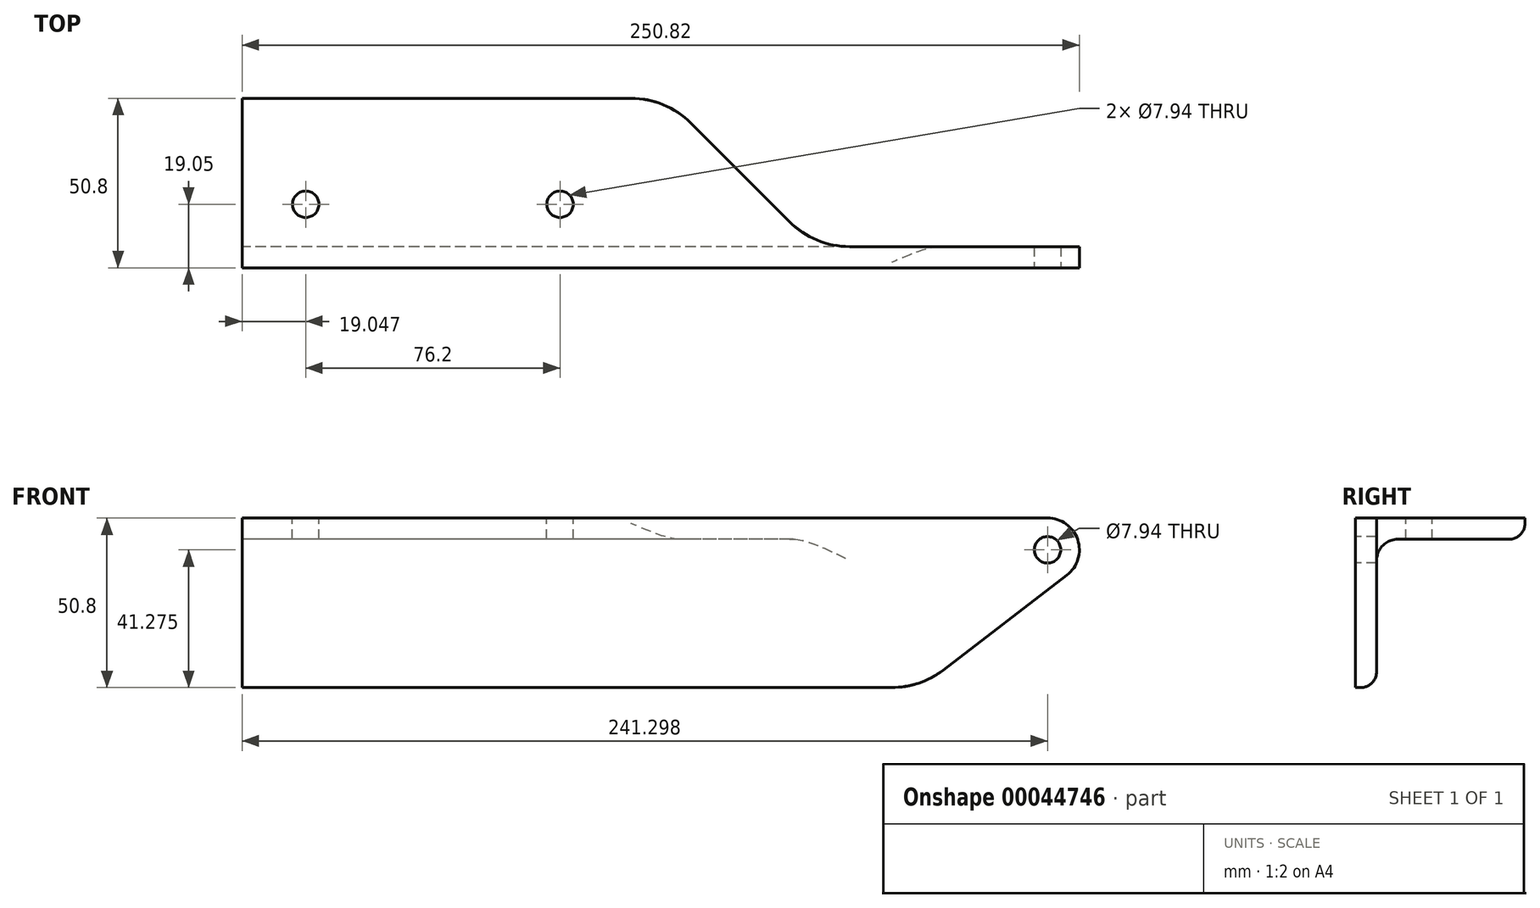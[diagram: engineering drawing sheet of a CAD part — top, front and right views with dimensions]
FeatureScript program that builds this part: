
annotation { "Feature Type Name" : "Feature", "Feature Type Description" : "" }
export const myFeature = defineFeature(function(context is Context, id is Id, definition is map)
    precondition{}
    {
        {
            var Q0;
            Q0=qCreatedBy(makeId("Right.planeOp"),FACE);
            var sketch = newSketch(context, id + "F0", { "sketchPlane" : qUnion([Q0])});
            skLineSegment(sketch, "E0", {"start": v(0, 0) * mm, "end": v(50.8, 0) * mm});
            skLineSegment(sketch, "E1", {"start": v(0, 0) * mm, "end": v(0, -50.8) * mm});
            skLineSegment(sketch, "E2.0", {"start": v(12.7, -6.35) * mm, "end": v(46.04, -6.35) * mm});
            skLineSegment(sketch, "E2.1", {"start": v(6.35, -12.7) * mm, "end": v(6.35, -46.04) * mm});
            skPoint(sketch, "E3.visualSharp", {"position": v(6.35, -6.35) * mm});
            skArc(sketch, "E3.filletArc", {"start": v(12.7, -6.35) * mm, "mid": v(8.2, -8.2) * mm, "end": v(6.35, -12.7) * mm});
            skLineSegment(sketch, "E4", {"start": v(1.59, -50.8) * mm, "end": v(0, -50.8) * mm});
            skLineSegment(sketch, "E5", {"start": v(50.8, -1.59) * mm, "end": v(50.8, 0) * mm});
            skPoint(sketch, "E6.visualSharp", {"position": v(50.8, -6.35) * mm});
            skArc(sketch, "E6.filletArc", {"start": v(46.04, -6.35) * mm, "mid": v(49.4, -4.96) * mm, "end": v(50.8, -1.59) * mm});
            skPoint(sketch, "E7.visualSharp", {"position": v(6.35, -50.8) * mm});
            skArc(sketch, "E7.filletArc", {"start": v(1.59, -50.8) * mm, "mid": v(4.96, -49.4) * mm, "end": v(6.35, -46.04) * mm});
            skSolve(sketch);
        }
        {
            var Q0;
            Q0 = qSketchRegion(id + "F0", true);
            extrude(context, id + "F1", {"entities" : qUnion([Q0]), "endBound" : BoundingType.SYMMETRIC, "depth" : 250.82 * mm});
        }
        {
            var Q0;
            Q0=makeQuery(id+"F1.opExtrude","SWEPT_FACE",FACE,{"disambiguationData":[OSD([sQuery(id+"F0.wireOp",EDGE,"E0")])]});
            var sketch = newSketch(context, id + "F2", { "sketchPlane" : qUnion([Q0])});
            skLineSegment(sketch, "E8.0", {"start": v(125.41, 0) * mm, "end": v(-125.41, 0) * mm, "construction": true});
            skLineSegment(sketch, "E9.0", {"start": v(125.41, 19.05) * mm, "end": v(-125.41, 19.05) * mm, "construction": true});
            skLineSegment(sketch, "E10.0", {"start": v(-125.41, 0) * mm, "end": v(-125.41, 50.8) * mm, "construction": true});
            skLineSegment(sketch, "E11.0", {"start": v(-106.36, 0) * mm, "end": v(-106.36, 50.8) * mm, "construction": true});
            skLineSegment(sketch, "E12.0", {"start": v(-30.16, 0) * mm, "end": v(-30.16, 50.8) * mm, "construction": true});
            skPoint(sketch, "E13", {"position": v(-106.36, 19.05) * mm});
            skPoint(sketch, "E14", {"position": v(-30.16, 19.05) * mm});
            skSolve(sketch);
        }
        {
            var Q0;
            Q0=sQuery(id+"F2.wireOp",VERTEX,"E13");
            var Q1;
            Q1=sQuery(id+"F2.wireOp",VERTEX,"E14");
            var Q2;
            Q2=makeQuery(id+"F1.opExtrude","SWEPT_BODY",BODY,{"disambiguationData":[OSD([sQuery(id+"F0.wireOp",EDGE,"E0"),sQuery(id+"F0.wireOp",EDGE,"E1"),sQuery(id+"F0.wireOp",EDGE,"E2.0"),sQuery(id+"F0.wireOp",EDGE,"E2.1"),sQuery(id+"F0.wireOp",EDGE,"E3.filletArc"),sQuery(id+"F0.wireOp",EDGE,"E4"),sQuery(id+"F0.wireOp",EDGE,"E5"),sQuery(id+"F0.wireOp",EDGE,"E6.filletArc"),sQuery(id+"F0.wireOp",EDGE,"E7.filletArc")])]});
            hole(context, id + "F3", {"style" : HoleStyle.SIMPLE, "holeDiameter" : 7.94 * mm, "endStyle" : HoleEndStyle.THROUGH, "locations" : qUnion([Q0, Q1]), "scope" : qUnion([Q2])});
        }
        {
            var Q0;
            Q0=makeQuery(id+"F1.opExtrude","SWEPT_FACE",FACE,{"disambiguationData":[OSD([sQuery(id+"F0.wireOp",EDGE,"E0")])]});
            var sketch = newSketch(context, id + "F4", { "sketchPlane" : qUnion([Q0])});
            skLineSegment(sketch, "E15.0", {"start": v(125.41, 6.35) * mm, "end": v(46.04, 6.35) * mm});
            skLineSegment(sketch, "E16.0", {"start": v(-125.41, 0) * mm, "end": v(-125.41, 50.8) * mm, "construction": true});
            skLineSegment(sketch, "E17.0", {"start": v(1.59, 0) * mm, "end": v(1.59, 50.8) * mm, "construction": true});
            skLineSegment(sketch, "E18.0", {"start": v(46.04, 0) * mm, "end": v(46.04, 50.8) * mm, "construction": true});
            skLineSegment(sketch, "E19", {"start": v(46.04, 6.35) * mm, "end": v(1.59, 50.8) * mm});
            skLineSegment(sketch, "E20", {"start": v(1.59, 50.8) * mm, "end": v(125.41, 50.8) * mm});
            skLineSegment(sketch, "E21", {"start": v(125.41, 50.8) * mm, "end": v(125.41, 6.35) * mm});
            skPoint(sketch, "E22.orphan", {"position": v(-125.41, 6.35) * mm});
            skSolve(sketch);
        }
        {
            var Q0;
            Q0 = qSketchRegion(id + "F4", true);
            extrude(context, id + "F5", {"entities" : qUnion([Q0]), "operationType" : NewBodyOperationType.REMOVE, "endBound" : BoundingType.THROUGH_ALL, "oppositeDirection" : true, "depth" : 25.4 * mm});
        }
        {
            var Q0;
            Q0=makeQuery(id+"F1.opExtrude","SWEPT_FACE",FACE,{"disambiguationData":[OSD([sQuery(id+"F0.wireOp",EDGE,"E0")])]});
            var sketch = newSketch(context, id + "F6", { "sketchPlane" : qUnion([Q0])});
            skLineSegment(sketch, "E23.0", {"start": v(-8.93, 50.8) * mm, "end": v(-125.41, 50.8) * mm});
            skLineSegment(sketch, "E24.0", {"start": v(46.04, 6.35) * mm, "end": v(9.03, 43.36) * mm});
            skLineSegment(sketch, "E25.rect.bottom", {"start": v(-21.33, 63.74) * mm, "end": v(24.5, 63.74) * mm});
            skLineSegment(sketch, "E25.rect.top", {"start": v(14.53, 37.86) * mm, "end": v(24.5, 37.86) * mm});
            skLineSegment(sketch, "E25.rect.left", {"start": v(-21.33, 63.74) * mm, "end": v(-21.33, 50.8) * mm});
            skLineSegment(sketch, "E25.rect.right", {"start": v(24.5, 63.74) * mm, "end": v(24.5, 37.86) * mm});
            skPoint(sketch, "E25.rect.middle", {"position": v(1.59, 50.8) * mm});
            skArc(sketch, "E26.filletArc", {"start": v(9.03, 43.36) * mm, "mid": v(0.79, 48.87) * mm, "end": v(-8.93, 50.8) * mm});
            skPoint(sketch, "E27.orphan", {"position": v(-21.33, 37.86) * mm});
            skSolve(sketch);
        }
        {
            var Q0;
            Q0 = qSketchRegion(id + "F6", true);
            extrude(context, id + "F7", {"entities" : qUnion([Q0]), "operationType" : NewBodyOperationType.REMOVE, "endBound" : BoundingType.THROUGH_ALL, "oppositeDirection" : true, "depth" : 25.4 * mm});
        }
        {
            var Q0;
            Q0=makeQuery(id+"F5.boolean.opBoolean","COPY",EDGE,{"derivedFrom":makeQuery(id+"F5.opExtrude","SWEPT_EDGE",EDGE,{"disambiguationData":[OSD([sQuery(id+"F4.wireOp",EDGE,"E15.0"),sQuery(id+"F4.wireOp",EDGE,"E19")])]})});
            fillet(context, id + "F8", {"entities" : qUnion([Q0]), "radius" : 25.4 * mm, "tangentPropagation" : true, "allowEdgeOverflow" : false});
        }
        {
            var Q0;
            Q0=makeQuery(id+"F1.opExtrude","SWEPT_FACE",FACE,{"disambiguationData":[OSD([sQuery(id+"F0.wireOp",EDGE,"E1")])]});
            var sketch = newSketch(context, id + "F9", { "sketchPlane" : qUnion([Q0])});
            skLineSegment(sketch, "E28.0", {"start": v(-125.41, 0) * mm, "end": v(-125.41, -50.8) * mm, "construction": true});
            skLineSegment(sketch, "E29.0", {"start": v(115.89, 0) * mm, "end": v(115.89, -50.8) * mm, "construction": true});
            skLineSegment(sketch, "E30.0", {"start": v(125.41, -9.53) * mm, "end": v(-125.41, -9.53) * mm, "construction": true});
            skArc(sketch, "E31", {"start": v(115.89, -19.05) * mm, "mid": v(125.41, -9.53) * mm, "end": v(115.89, 0) * mm});
            skLineSegment(sketch, "E32.0", {"start": v(77.79, 0) * mm, "end": v(77.79, -50.8) * mm});
            skLineSegment(sketch, "E33.0", {"start": v(125.41, -50.8) * mm, "end": v(-125.41, -50.8) * mm});
            skLineSegment(sketch, "E34", {"start": v(77.79, -50.8) * mm, "end": v(121.69, -17.08) * mm});
            skLineSegment(sketch, "E35", {"start": v(115.89, 0) * mm, "end": v(115.89, 14.21) * mm});
            skLineSegment(sketch, "E36", {"start": v(115.89, 14.21) * mm, "end": v(141.57, 14.21) * mm});
            skLineSegment(sketch, "E37", {"start": v(141.57, 14.21) * mm, "end": v(141.57, -61.2) * mm});
            skLineSegment(sketch, "E38", {"start": v(141.57, -61.2) * mm, "end": v(77.79, -61.2) * mm});
            skLineSegment(sketch, "E39", {"start": v(77.79, -61.2) * mm, "end": v(77.79, -50.8) * mm});
            skSolve(sketch);
        }
        {
            var Q0;
            Q0 = qSketchRegion(id + "F9", true);
            extrude(context, id + "F10", {"entities" : qUnion([Q0]), "operationType" : NewBodyOperationType.REMOVE, "endBound" : BoundingType.THROUGH_ALL, "oppositeDirection" : true, "depth" : 25.4 * mm});
        }
        {
            var Q0;
            {var subQ2=sQuery(id+"F9.wireOp",EDGE,"E32.0");Q0=makeQuery(id+"F9.imprint","IMPRINT",FACE,{"disambiguationData":[TD([[makeQuery(id+"F9.imprint","IMPRINT",EDGE,{"derivedFrom":subQ2}),1.0]])]});}
            var sketch = newSketch(context, id + "F11", { "sketchPlane" : qUnion([Q0])});
            skLineSegment(sketch, "E40.0", {"start": v(125.41, -9.53) * mm, "end": v(-125.41, -9.53) * mm, "construction": true});
            skLineSegment(sketch, "E41.0", {"start": v(115.89, 0) * mm, "end": v(115.89, -50.8) * mm, "construction": true});
            skPoint(sketch, "E42", {"position": v(115.89, -9.53) * mm});
            skSolve(sketch);
        }
        {
            var Q0;
            Q0=sQuery(id+"F11.wireOp",VERTEX,"E42");
            var Q1;
            Q1=makeQuery(id+"F1.opExtrude","SWEPT_BODY",BODY,{"disambiguationData":[OSD([sQuery(id+"F0.wireOp",EDGE,"E0"),sQuery(id+"F0.wireOp",EDGE,"E1"),sQuery(id+"F0.wireOp",EDGE,"E2.0"),sQuery(id+"F0.wireOp",EDGE,"E2.1"),sQuery(id+"F0.wireOp",EDGE,"E3.filletArc"),sQuery(id+"F0.wireOp",EDGE,"E4"),sQuery(id+"F0.wireOp",EDGE,"E5"),sQuery(id+"F0.wireOp",EDGE,"E6.filletArc"),sQuery(id+"F0.wireOp",EDGE,"E7.filletArc")])]});
            hole(context, id + "F12", {"style" : HoleStyle.SIMPLE, "holeDiameter" : 7.94 * mm, "endStyle" : HoleEndStyle.THROUGH, "locations" : qUnion([Q0]), "scope" : qUnion([Q1])});
        }
        {
            var Q0;
            Q0=makeQuery(id+"F1.opExtrude","SWEPT_FACE",FACE,{"disambiguationData":[OSD([sQuery(id+"F0.wireOp",EDGE,"E1")])]});
            var sketch = newSketch(context, id + "F13", { "sketchPlane" : qUnion([Q0])});
            skLineSegment(sketch, "E43.0", {"start": v(84.63, -45.54) * mm, "end": v(92.94, -39.16) * mm});
            skLineSegment(sketch, "E44.0", {"start": v(69.16, -50.8) * mm, "end": v(57.52, -50.8) * mm});
            skPoint(sketch, "E45.visualSharp", {"position": v(77.79, -50.8) * mm});
            skArc(sketch, "E45.filletArc", {"start": v(69.16, -50.8) * mm, "mid": v(77.33, -49.45) * mm, "end": v(84.63, -45.54) * mm});
            skLineSegment(sketch, "E46.rect.bottom", {"start": v(92.94, -39.16) * mm, "end": v(98.06, -39.16) * mm});
            skLineSegment(sketch, "E46.rect.top", {"start": v(57.52, -62.44) * mm, "end": v(98.06, -62.44) * mm});
            skLineSegment(sketch, "E46.rect.left", {"start": v(57.52, -50.8) * mm, "end": v(57.52, -62.44) * mm});
            skLineSegment(sketch, "E46.rect.right", {"start": v(98.06, -39.16) * mm, "end": v(98.06, -62.44) * mm});
            skPoint(sketch, "E47.orphan", {"position": v(57.52, -39.16) * mm});
            skPoint(sketch, "E48.orphan", {"position": v(-125.41, -50.8) * mm});
            skPoint(sketch, "E49.orphan", {"position": v(121.69, -17.08) * mm});
            skSolve(sketch);
        }
        {
            var Q0;
            Q0 = qSketchRegion(id + "F13", true);
            extrude(context, id + "F14", {"entities" : qUnion([Q0]), "operationType" : NewBodyOperationType.REMOVE, "endBound" : BoundingType.THROUGH_ALL, "oppositeDirection" : true, "depth" : 25.4 * mm});
        }
    });
